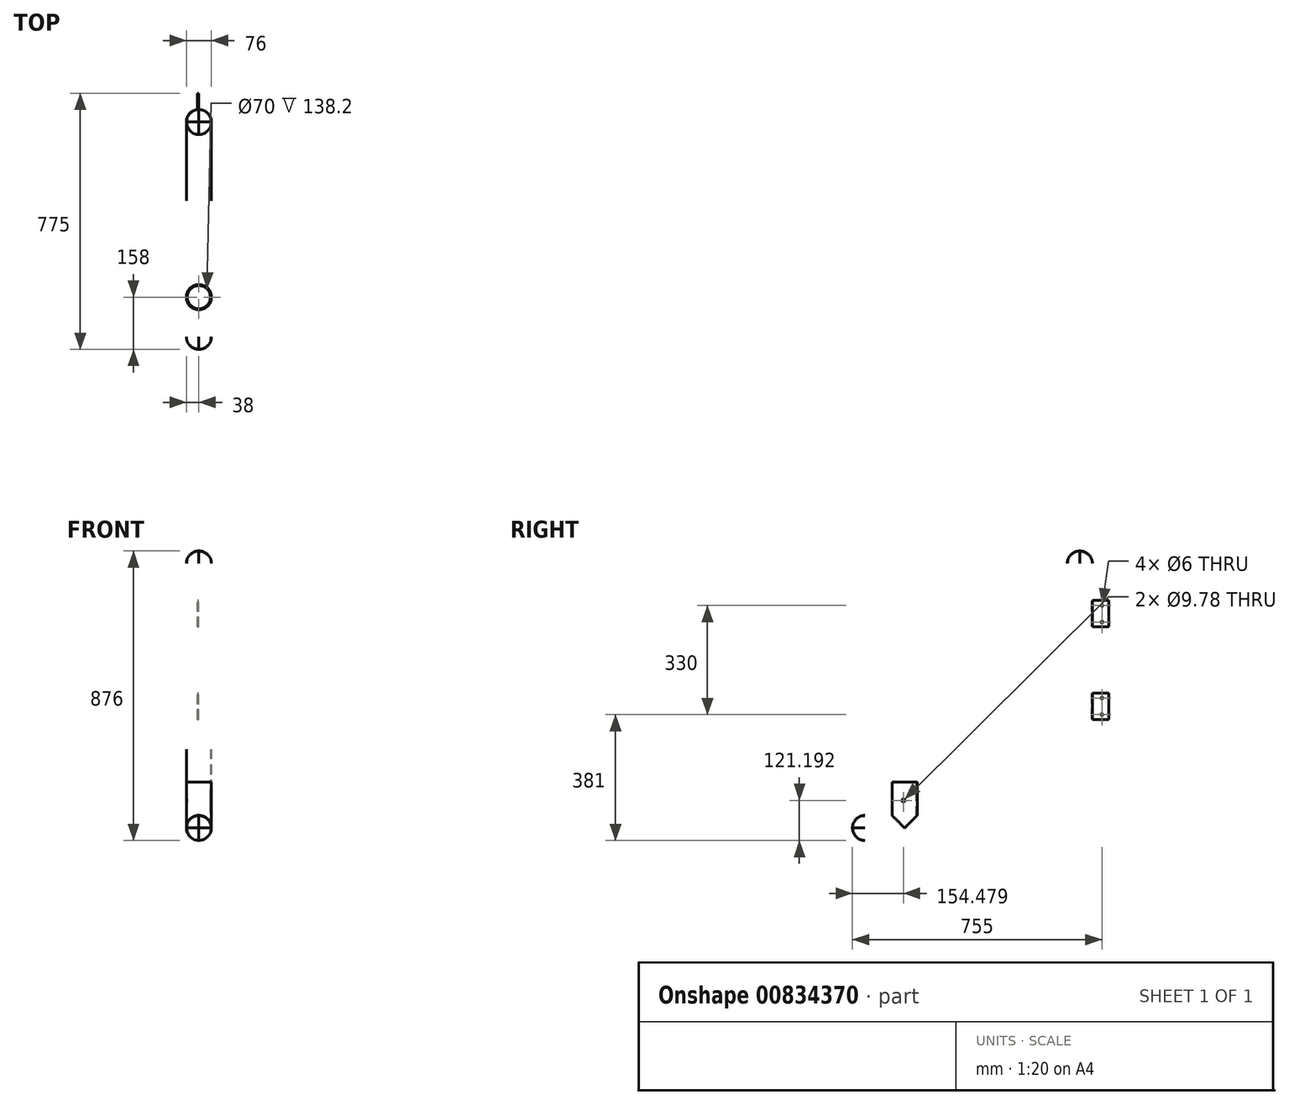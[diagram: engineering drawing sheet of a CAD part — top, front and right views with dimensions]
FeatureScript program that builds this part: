
annotation { "Feature Type Name" : "Feature", "Feature Type Description" : "" }
export const myFeature = defineFeature(function(context is Context, id is Id, definition is map)
    precondition{}
    {
        {
            var Q0;
            Q0=qCreatedBy(makeId("Right.planeOp"),FACE);
            var sketch = newSketch(context, id + "F0", { "sketchPlane" : qUnion([Q0])});
            skLineSegment(sketch, "E0", {"start": v(0, 199.8) * mm, "end": v(0, 799.8) * mm});
            skLineSegment(sketch, "E1", {"start": v(-200, -0.2) * mm, "end": v(-650, -0.2) * mm});
            skArc(sketch, "E2", {"start": v(-200, -0.2) * mm, "mid": v(-58.58, 58.38) * mm, "end": v(0, 199.8) * mm});
            skLineSegment(sketch, "E3", {"start": v(0, 799.8) * mm, "end": v(76, 799.8) * mm});
            skLineSegment(sketch, "E4.0", {"start": v(76, 199.8) * mm, "end": v(76, 799.8) * mm});
            skArc(sketch, "E4.1", {"start": v(-200, -76.2) * mm, "mid": v(-4.84, 4.64) * mm, "end": v(76, 199.8) * mm});
            skLineSegment(sketch, "E4.2", {"start": v(-200, -76.2) * mm, "end": v(-650, -76.2) * mm});
            skLineSegment(sketch, "E5", {"start": v(-650, -0.2) * mm, "end": v(-650, -76.2) * mm});
            skSolve(sketch);
        }
        {
            var Q0;
            Q0=makeQuery(id+"F0.imprint","IMPRINT",FACE,{"disambiguationData":[TD([[makeQuery(id+"F0.imprint","IMPRINT",EDGE,{"derivedFrom":sQuery(id+"F0.wireOp",EDGE,"E0")}),-1.0]])]});
            extrude(context, id + "F1", {"entities" : qUnion([Q0]), "depth" : 76 * mm, "offsetDistance" : 25.4 * mm});
        }
        {
            var Q0;
            Q0=makeQuery(id+"F1.opExtrude","CAP_EDGE",EDGE,{"disambiguationData":[OSD([sQuery(id+"F0.wireOp",EDGE,"E0")])],"isStart":false});
            var Q1;
            Q1=makeQuery(id+"F1.opExtrude","CAP_EDGE",EDGE,{"disambiguationData":[OSD([sQuery(id+"F0.wireOp",EDGE,"E0")])],"isStart":true});
            var Q2;
            Q2=makeQuery(id+"F1.opExtrude","CAP_EDGE",EDGE,{"disambiguationData":[OSD([sQuery(id+"F0.wireOp",EDGE,"E2")])],"isStart":false});
            var Q3;
            Q3=makeQuery(id+"F1.opExtrude","CAP_EDGE",EDGE,{"disambiguationData":[OSD([sQuery(id+"F0.wireOp",EDGE,"E2")])],"isStart":true});
            var Q4;
            Q4=makeQuery(id+"F1.opExtrude","CAP_EDGE",EDGE,{"disambiguationData":[OSD([sQuery(id+"F0.wireOp",EDGE,"E1")])],"isStart":false});
            var Q5;
            Q5=makeQuery(id+"F1.opExtrude","CAP_EDGE",EDGE,{"disambiguationData":[OSD([sQuery(id+"F0.wireOp",EDGE,"E1")])],"isStart":true});
            var Q6;
            Q6=makeQuery(id+"F1.opExtrude","CAP_EDGE",EDGE,{"disambiguationData":[OSD([sQuery(id+"F0.wireOp",EDGE,"E4.2")])],"isStart":false});
            var Q7;
            Q7=makeQuery(id+"F1.opExtrude","CAP_EDGE",EDGE,{"disambiguationData":[OSD([sQuery(id+"F0.wireOp",EDGE,"E4.1")])],"isStart":false});
            var Q8;
            Q8=makeQuery(id+"F1.opExtrude","CAP_EDGE",EDGE,{"disambiguationData":[OSD([sQuery(id+"F0.wireOp",EDGE,"E4.0")])],"isStart":false});
            var Q9;
            Q9=makeQuery(id+"F1.opExtrude","CAP_EDGE",EDGE,{"disambiguationData":[OSD([sQuery(id+"F0.wireOp",EDGE,"E4.0")])],"isStart":true});
            var Q10;
            Q10=makeQuery(id+"F1.opExtrude","CAP_EDGE",EDGE,{"disambiguationData":[OSD([sQuery(id+"F0.wireOp",EDGE,"E4.1")])],"isStart":true});
            var Q11;
            Q11=makeQuery(id+"F1.opExtrude","CAP_EDGE",EDGE,{"disambiguationData":[OSD([sQuery(id+"F0.wireOp",EDGE,"E4.2")])],"isStart":true});
            fillet(context, id + "F2", {"entities" : qUnion([Q0, Q1, Q2, Q3, Q4, Q5, Q6, Q7, Q8, Q9, Q10, Q11]), "radius" : 38.1 * mm, "tangentPropagation" : true, "allowEdgeOverflow" : false});
        }
        {
            var Q0;
            Q0=makeQuery(id+"F1.opExtrude","SWEPT_FACE",FACE,{"disambiguationData":[OSD([sQuery(id+"F0.wireOp",EDGE,"E5")])]});
            fillet(context, id + "F3", {"entities" : qUnion([Q0]), "radius" : 37.85 * mm, "tangentPropagation" : true, "allowEdgeOverflow" : false});
        }
        {
            var Q0;
            Q0=qCreatedBy(makeId("Top.planeOp"),FACE);
            cPlane(context, id + "F4", {"entities" : qUnion([Q0]), "cplaneType" : CPlaneType.OFFSET, "offset" : 100 * mm, "width" : 152.4 * mm, "height" : 152.4 * mm});
        }
        {
            var Q0;
            Q0=qCreatedBy(id+"F4.planeOp",FACE);
            var sketch = newSketch(context, id + "F5", { "sketchPlane" : qUnion([Q0])});
            skLineSegment(sketch, "E6.0", {"start": v(76, -200) * mm, "end": v(76, -612.15) * mm});
            skLineSegment(sketch, "E7.0", {"start": v(0, -612.15) * mm, "end": v(0, -200) * mm});
            skPoint(sketch, "E8.0", {"position": v(38, -650) * mm});
            skLineSegment(sketch, "E9", {"start": v(0, -530) * mm, "end": v(0, -454) * mm});
            skCircle(sketch, "E10", {"center": v(38, -492) * mm, "radius": 38 * mm});
            skSolve(sketch);
        }
        {
            var Q0;
            Q0=makeQuery(id+"F5.imprint","IMPRINT",FACE,{"disambiguationData":[TD([[makeQuery(id+"F5.imprint","IMPRINT",EDGE,{"derivedFrom":sQuery(id+"F5.wireOp",EDGE,"E10")}),1.0]])]});
            extrude(context, id + "F6", {"entities" : qUnion([Q0]), "operationType" : NewBodyOperationType.ADD, "endBound" : BoundingType.UP_TO_NEXT, "oppositeDirection" : true, "depth" : 25.4 * mm, "offsetDistance" : 25.4 * mm});
        }
        {
            var Q0;
            Q0=qCreatedBy(makeId("Front.planeOp"),FACE);
            cPlane(context, id + "F7", {"entities" : qUnion([Q0]), "cplaneType" : CPlaneType.OFFSET, "offset" : 125 * mm, "oppositeDirection" : true, "width" : 152.4 * mm, "height" : 152.4 * mm});
        }
        {
            var Q0;
            Q0=qCreatedBy(id+"F7.planeOp",FACE);
            var sketch = newSketch(context, id + "F8", { "sketchPlane" : qUnion([Q0])});
            skLineSegment(sketch, "E11.0.0", {"start": v(38, 199.8) * mm, "end": v(0, 199.8) * mm});
            skLineSegment(sketch, "E11.0.1", {"start": v(0, 199.8) * mm, "end": v(0, 799.8) * mm});
            skLineSegment(sketch, "E11.0.2", {"start": v(0, 799.8) * mm, "end": v(38, 799.8) * mm});
            skLineSegment(sketch, "E11.0.3", {"start": v(38, 799.8) * mm, "end": v(38, 199.8) * mm});
            skLineSegment(sketch, "E12.0.0", {"start": v(76, 799.8) * mm, "end": v(76, 199.8) * mm});
            skLineSegment(sketch, "E12.0.1", {"start": v(76, 199.8) * mm, "end": v(38, 199.8) * mm});
            skLineSegment(sketch, "E12.0.2", {"start": v(38, 199.8) * mm, "end": v(38, 799.8) * mm});
            skLineSegment(sketch, "E12.0.3", {"start": v(38, 799.8) * mm, "end": v(76, 799.8) * mm});
            skLineSegment(sketch, "E13.bottom", {"start": v(38, 649.8) * mm, "end": v(33, 649.8) * mm});
            skLineSegment(sketch, "E13.top", {"start": v(38, 569.8) * mm, "end": v(33, 569.8) * mm});
            skLineSegment(sketch, "E13.left", {"start": v(38, 649.8) * mm, "end": v(38, 569.8) * mm});
            skLineSegment(sketch, "E13.right", {"start": v(33, 649.8) * mm, "end": v(33, 569.8) * mm});
            skLineSegment(sketch, "E14.bottom", {"start": v(38, 369.8) * mm, "end": v(33, 369.8) * mm});
            skLineSegment(sketch, "E14.top", {"start": v(38, 289.8) * mm, "end": v(33, 289.8) * mm});
            skLineSegment(sketch, "E14.left", {"start": v(38, 369.8) * mm, "end": v(38, 289.8) * mm});
            skLineSegment(sketch, "E14.right", {"start": v(33, 369.8) * mm, "end": v(33, 289.8) * mm});
            skSolve(sketch);
        }
        {
            var Q0;
            Q0=makeQuery(id+"F8.imprint","IMPRINT",FACE,{"disambiguationData":[TD([[makeQuery(id+"F8.imprint","IMPRINT",EDGE,{"derivedFrom":sQuery(id+"F8.wireOp",EDGE,"E13.bottom")}),1.0]])]});
            var Q1;
            Q1=makeQuery(id+"F8.imprint","IMPRINT",FACE,{"disambiguationData":[TD([[makeQuery(id+"F8.imprint","IMPRINT",EDGE,{"derivedFrom":sQuery(id+"F8.wireOp",EDGE,"E14.bottom")}),1.0]])]});
            extrude(context, id + "F9", {"entities" : qUnion([Q0, Q1]), "operationType" : NewBodyOperationType.ADD, "endBound" : BoundingType.UP_TO_NEXT, "depth" : 25.4 * mm, "offsetDistance" : 25.4 * mm});
        }
        {
            var Q0;
            Q0=makeQuery(id+"F9.opExtrude","SWEPT_FACE",FACE,{"disambiguationData":[OSD([sQuery(id+"F8.wireOp",EDGE,"E13.right")])]});
            var sketch = newSketch(context, id + "F10", { "sketchPlane" : qUnion([Q0])});
            skLineSegment(sketch, "E15.0.0", {"start": v(-125, 569.8) * mm, "end": v(-75.66, 569.8) * mm});
            skLineSegment(sketch, "E15.0.1", {"start": v(-75.66, 569.8) * mm, "end": v(-75.66, 649.8) * mm});
            skLineSegment(sketch, "E15.0.2", {"start": v(-75.66, 649.8) * mm, "end": v(-125, 649.8) * mm});
            skLineSegment(sketch, "E15.0.3", {"start": v(-125, 649.8) * mm, "end": v(-125, 569.8) * mm});
            skLineSegment(sketch, "E16.0.0", {"start": v(-125, 289.8) * mm, "end": v(-75.66, 289.8) * mm});
            skLineSegment(sketch, "E16.0.1", {"start": v(-75.66, 289.8) * mm, "end": v(-75.66, 369.8) * mm});
            skLineSegment(sketch, "E16.0.2", {"start": v(-75.66, 369.8) * mm, "end": v(-125, 369.8) * mm});
            skLineSegment(sketch, "E16.0.3", {"start": v(-125, 369.8) * mm, "end": v(-125, 289.8) * mm});
            skCircle(sketch, "E17", {"center": v(-105, 634.8) * mm, "radius": 3 * mm});
            skCircle(sketch, "E18", {"center": v(-105, 584.8) * mm, "radius": 3 * mm});
            skCircle(sketch, "E19", {"center": v(-105, 354.8) * mm, "radius": 3 * mm});
            skCircle(sketch, "E20", {"center": v(-105, 304.8) * mm, "radius": 3 * mm});
            skSolve(sketch);
        }
        {
            var Q0;
            Q0=makeQuery(id+"F10.imprint","IMPRINT",FACE,{"disambiguationData":[TD([[makeQuery(id+"F10.imprint","IMPRINT",EDGE,{"derivedFrom":sQuery(id+"F10.wireOp",EDGE,"E17")}),1.0]])]});
            var Q1;
            Q1=makeQuery(id+"F10.imprint","IMPRINT",FACE,{"disambiguationData":[TD([[makeQuery(id+"F10.imprint","IMPRINT",EDGE,{"derivedFrom":sQuery(id+"F10.wireOp",EDGE,"E18")}),1.0]])]});
            var Q2;
            Q2=makeQuery(id+"F10.imprint","IMPRINT",FACE,{"disambiguationData":[TD([[makeQuery(id+"F10.imprint","IMPRINT",EDGE,{"derivedFrom":sQuery(id+"F10.wireOp",EDGE,"E19")}),1.0]])]});
            var Q3;
            Q3=makeQuery(id+"F10.imprint","IMPRINT",FACE,{"disambiguationData":[TD([[makeQuery(id+"F10.imprint","IMPRINT",EDGE,{"derivedFrom":sQuery(id+"F10.wireOp",EDGE,"E20")}),1.0]])]});
            extrude(context, id + "F11", {"entities" : qUnion([Q0, Q1, Q2, Q3]), "operationType" : NewBodyOperationType.REMOVE, "oppositeDirection" : true, "depth" : 25.4 * mm, "offsetDistance" : 25.4 * mm});
        }
        {
            var Q0;
            Q0=makeQuery(id+"F2.opFillet","BLEND_EDGE",EDGE,{"blendedFrom":[makeQuery(id+"F1.opExtrude","CAP_EDGE",EDGE,{"disambiguationData":[OSD([sQuery(id+"F0.wireOp",EDGE,"E0")])],"isStart":true}),makeQuery(id+"F1.opExtrude","SWEPT_FACE",FACE,{"disambiguationData":[OSD([sQuery(id+"F0.wireOp",EDGE,"E3")])]})],"blendedInto":[makeQuery(id+"F1.opExtrude","SWEPT_FACE",FACE,{"disambiguationData":[OSD([sQuery(id+"F0.wireOp",EDGE,"E3")])]})]});
            var Q1;
            Q1=makeQuery(id+"F1.opExtrude","SWEPT_FACE",FACE,{"disambiguationData":[OSD([sQuery(id+"F0.wireOp",EDGE,"E3")])]});
            fillet(context, id + "F12", {"entities" : qUnion([Q0, Q1]), "radius" : 37.85 * mm, "tangentPropagation" : true, "allowEdgeOverflow" : false});
        }
        {
            var Q0;
            Q0=makeQuery(id+"F6.opExtrude","CAP_FACE",FACE,{"disambiguationData":[OSD([sQuery(id+"F5.wireOp",EDGE,"E10")])],"isStart":true});
            shell(context, id + "F13", {"entities" : qUnion([Q0]), "thickness" : 3 * mm});
        }
        {
            var Q0;
            Q0=qCreatedBy(makeId("Right.planeOp"),FACE);
            var sketch = newSketch(context, id + "F14", { "sketchPlane" : qUnion([Q0])});
            skLineSegment(sketch, "E21", {"start": v(-457, 100) * mm, "end": v(-457, -3.2) * mm});
            skLineSegment(sketch, "E22", {"start": v(-527, -3.2) * mm, "end": v(-527, 100) * mm});
            skLineSegment(sketch, "E23.0", {"start": v(-530, 100) * mm, "end": v(-454, 100) * mm});
            skLineSegment(sketch, "E24", {"start": v(-454, 100) * mm, "end": v(-441.92, 100) * mm});
            skLineSegment(sketch, "E25", {"start": v(-441.92, 100) * mm, "end": v(-441.92, 45) * mm});
            skLineSegment(sketch, "E26", {"start": v(-441.92, 45) * mm, "end": v(-549.12, 45) * mm});
            skLineSegment(sketch, "E27", {"start": v(-549.12, 45) * mm, "end": v(-549.12, 100) * mm});
            skLineSegment(sketch, "E28", {"start": v(-549.12, 100) * mm, "end": v(-441.92, 100) * mm});
            skCircle(sketch, "E29", {"center": v(-495.52, 45) * mm, "radius": 4.9 * mm});
            skSolve(sketch);
        }
        {
            var Q0;
            {var subQ0=sQuery(id+"F14.wireOp",EDGE,"E29");var subQ1=sQuery(id+"F14.wireOp",EDGE,"E26");var subQ2=makeQuery(id+"F14.imprint","INTERSECT",VERTEX,{"disambiguationData":[OD(0.0)],"derivedFrom":[subQ1,subQ0]});Q0=makeQuery(id+"F14.imprint","IMPRINT",FACE,{"disambiguationData":[TD([[makeQuery(id+"F14.imprint","IMPRINT",EDGE,{"disambiguationData":[TD([[subQ2,-1.0]])],"derivedFrom":subQ1}),1.0]])]});}
            var Q1;
            {var subQ0=sQuery(id+"F14.wireOp",EDGE,"E29");var subQ1=sQuery(id+"F14.wireOp",EDGE,"E26");var subQ2=makeQuery(id+"F14.imprint","INTERSECT",VERTEX,{"disambiguationData":[OD(0.0)],"derivedFrom":[subQ1,subQ0]});Q1=makeQuery(id+"F14.imprint","IMPRINT",FACE,{"disambiguationData":[TD([[makeQuery(id+"F14.imprint","IMPRINT",EDGE,{"disambiguationData":[TD([[subQ2,-1.0]])],"derivedFrom":subQ1}),-1.0]])]});}
            extrude(context, id + "F15", {"entities" : qUnion([Q0, Q1]), "operationType" : NewBodyOperationType.REMOVE, "endBound" : BoundingType.SYMMETRIC, "oppositeDirection" : true, "depth" : 239.78 * mm, "offsetDistance" : 25.4 * mm});
        }
    });
